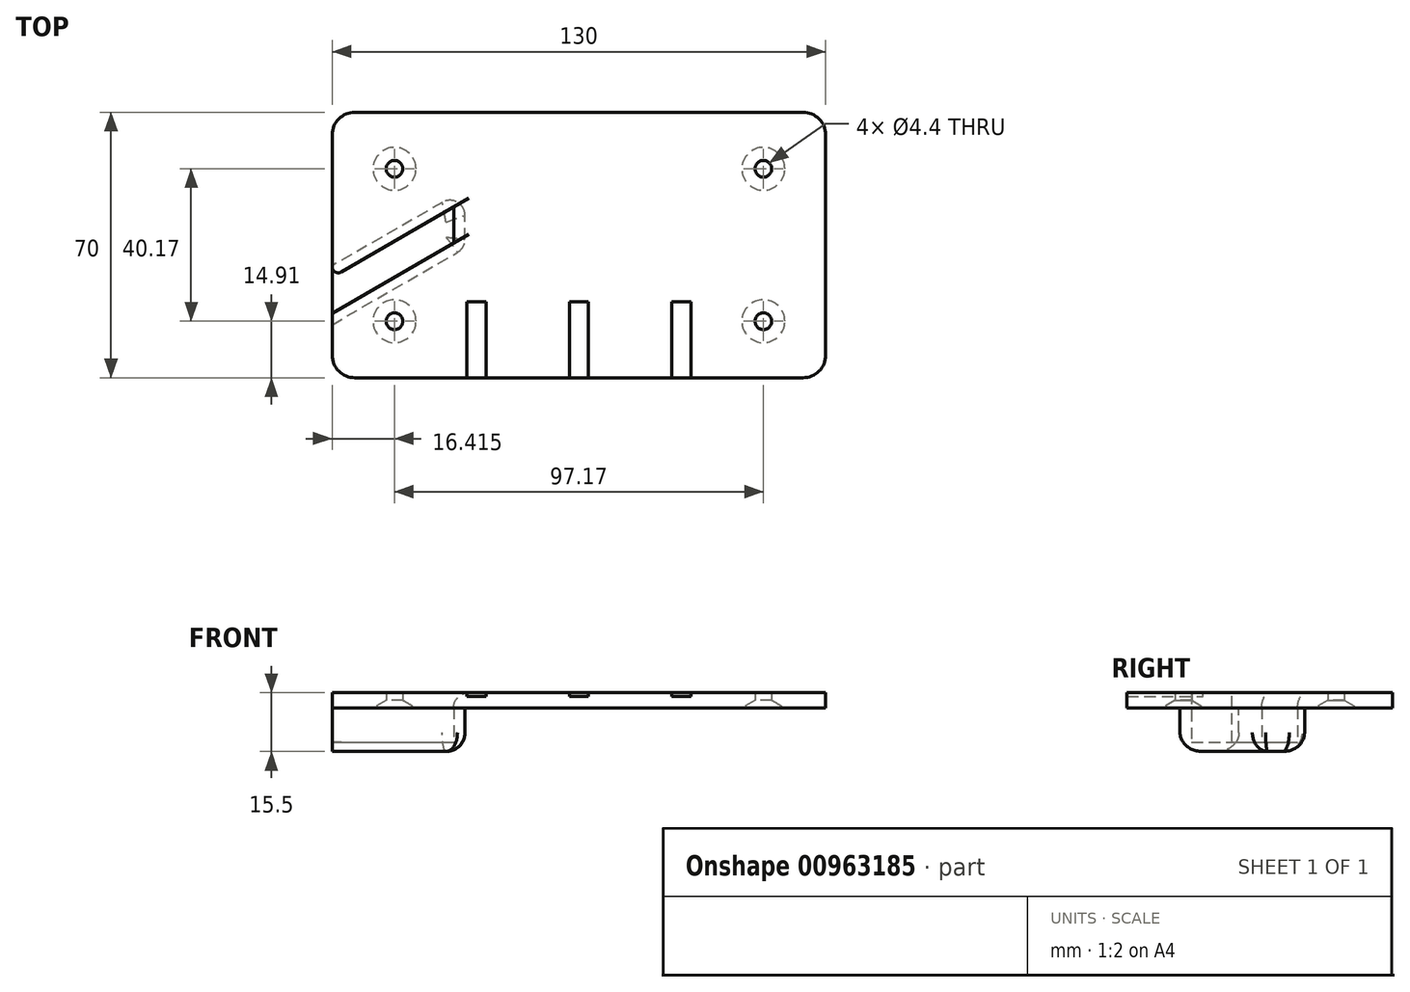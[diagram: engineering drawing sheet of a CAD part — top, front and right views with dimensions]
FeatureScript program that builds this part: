
annotation { "Feature Type Name" : "Feature", "Feature Type Description" : "" }
export const myFeature = defineFeature(function(context is Context, id is Id, definition is map)
    precondition{}
    {
        {
            var Q0;
            Q0=qCreatedBy(makeId("Top.planeOp"),FACE);
            var sketch = newSketch(context, id + "F0", { "sketchPlane" : qUnion([Q0])});
            skLineSegment(sketch, "E0.bottom", {"start": v(-46.53, -21.36) * mm, "end": v(71.47, -21.36) * mm});
            skLineSegment(sketch, "E0.top", {"start": v(-46.53, 48.64) * mm, "end": v(71.47, 48.64) * mm});
            skLineSegment(sketch, "E0.left", {"start": v(-52.53, -15.36) * mm, "end": v(-52.53, 42.64) * mm});
            skLineSegment(sketch, "E0.right", {"start": v(77.47, -15.36) * mm, "end": v(77.47, 42.64) * mm});
            skPoint(sketch, "E1.visualSharp", {"position": v(-52.53, 48.64) * mm});
            skArc(sketch, "E1.filletArc", {"start": v(-46.53, 48.64) * mm, "mid": v(-50.77, 46.88) * mm, "end": v(-52.53, 42.64) * mm});
            skPoint(sketch, "E2.visualSharp", {"position": v(77.47, 48.64) * mm});
            skArc(sketch, "E2.filletArc", {"start": v(77.47, 42.64) * mm, "mid": v(75.71, 46.88) * mm, "end": v(71.47, 48.64) * mm});
            skPoint(sketch, "E3.visualSharp", {"position": v(77.47, -21.36) * mm});
            skArc(sketch, "E3.filletArc", {"start": v(71.47, -21.36) * mm, "mid": v(75.71, -19.6) * mm, "end": v(77.47, -15.36) * mm});
            skPoint(sketch, "E4.visualSharp", {"position": v(-52.53, -21.36) * mm});
            skArc(sketch, "E4.filletArc", {"start": v(-52.53, -15.36) * mm, "mid": v(-50.77, -19.6) * mm, "end": v(-46.53, -21.36) * mm});
            skPoint(sketch, "E5", {"position": v(-36.11, 33.72) * mm});
            skPoint(sketch, "E6", {"position": v(61.06, 33.72) * mm});
            skPoint(sketch, "E7", {"position": v(61.06, -6.45) * mm});
            skPoint(sketch, "E8", {"position": v(-36.11, -6.45) * mm});
            skPoint(sketch, "E9", {"position": v(12.47, -6.45) * mm});
            skPoint(sketch, "E10", {"position": v(61.06, 13.64) * mm});
            skPoint(sketch, "E11", {"position": v(12.47, -21.36) * mm});
            skPoint(sketch, "E12", {"position": v(77.47, 13.64) * mm});
            skCircle(sketch, "E13", {"center": v(61.06, -6.45) * mm, "radius": 2.2 * mm});
            skCircle(sketch, "E14", {"center": v(61.06, 33.72) * mm, "radius": 2.2 * mm});
            skCircle(sketch, "E15", {"center": v(-36.11, 33.72) * mm, "radius": 2.2 * mm});
            skCircle(sketch, "E16", {"center": v(-36.11, -6.45) * mm, "radius": 2.2 * mm});
            skLineSegment(sketch, "E17", {"start": v(-52.53, -4.36) * mm, "end": v(-20.53, 14.11) * mm});
            skLineSegment(sketch, "E18", {"start": v(-52.53, 5.14) * mm, "end": v(-20.53, 23.61) * mm});
            skLineSegment(sketch, "E19", {"start": v(-20.53, 14.11) * mm, "end": v(-20.53, 23.61) * mm});
            skSolve(sketch);
        }
        {
            var Q0;
            Q0=makeQuery(id+"F0.imprint","IMPRINT",FACE,{"disambiguationData":[TD([[makeQuery(id+"F0.imprint","IMPRINT",EDGE,{"derivedFrom":sQuery(id+"F0.wireOp",EDGE,"E0.bottom")}),1.0]])]});
            extrude(context, id + "F1", {"entities" : qUnion([Q0]), "depth" : 4 * mm, "offsetDistance" : 25 * mm});
        }
        {
            var Q0;
            Q0=makeQuery(id+"F1.opExtrude","CAP_FACE",FACE,{"disambiguationData":[OSD([sQuery(id+"F0.wireOp",EDGE,"E0.bottom"),sQuery(id+"F0.wireOp",EDGE,"E0.top"),sQuery(id+"F0.wireOp",EDGE,"E0.left"),sQuery(id+"F0.wireOp",EDGE,"E0.right"),sQuery(id+"F0.wireOp",EDGE,"E1.filletArc"),sQuery(id+"F0.wireOp",EDGE,"E2.filletArc"),sQuery(id+"F0.wireOp",EDGE,"E3.filletArc"),sQuery(id+"F0.wireOp",EDGE,"E4.filletArc"),sQuery(id+"F0.wireOp",EDGE,"E13"),sQuery(id+"F0.wireOp",EDGE,"E14"),sQuery(id+"F0.wireOp",EDGE,"E15"),sQuery(id+"F0.wireOp",EDGE,"E16"),sQuery(id+"F0.wireOp",EDGE,"E17"),sQuery(id+"F0.wireOp",EDGE,"E18"),sQuery(id+"F0.wireOp",EDGE,"E19")])],"isStart":true});
            var sketch = newSketch(context, id + "F2", { "sketchPlane" : qUnion([Q0])});
            skLineSegment(sketch, "E20", {"start": v(-52.53, 7.36) * mm, "end": v(-17.53, -12.84) * mm});
            skLineSegment(sketch, "E21", {"start": v(-17.53, -12.84) * mm, "end": v(-17.53, -28.34) * mm});
            skLineSegment(sketch, "E22", {"start": v(-17.53, -28.34) * mm, "end": v(-52.53, -8.14) * mm});
            skLineSegment(sketch, "E23", {"start": v(-52.53, -8.14) * mm, "end": v(-52.53, -5.14) * mm});
            skLineSegment(sketch, "E24", {"start": v(-52.53, -5.14) * mm, "end": v(-20.53, -23.61) * mm});
            skLineSegment(sketch, "E25", {"start": v(-20.53, -23.61) * mm, "end": v(-20.53, -14.11) * mm});
            skLineSegment(sketch, "E26", {"start": v(-20.53, -14.11) * mm, "end": v(-52.53, 4.36) * mm});
            skLineSegment(sketch, "E27", {"start": v(-52.53, 4.36) * mm, "end": v(-52.53, 7.36) * mm});
            skSolve(sketch);
        }
        {
            var Q0;
            Q0=makeQuery(id+"F2.imprint","IMPRINT",FACE,{"disambiguationData":[TD([[makeQuery(id+"F2.imprint","IMPRINT",EDGE,{"derivedFrom":sQuery(id+"F2.wireOp",EDGE,"E20")}),-1.0]])]});
            extrude(context, id + "F3", {"entities" : qUnion([Q0]), "operationType" : NewBodyOperationType.ADD, "depth" : 9 * mm, "offsetDistance" : 25 * mm});
        }
        {
            var Q0;
            Q0=makeQuery(id+"F1.opExtrude","CAP_EDGE",EDGE,{"disambiguationData":[OSD([sQuery(id+"F0.wireOp",EDGE,"E15")])],"isStart":true});
            var Q1;
            Q1=makeQuery(id+"F1.opExtrude","CAP_EDGE",EDGE,{"disambiguationData":[OSD([sQuery(id+"F0.wireOp",EDGE,"E16")])],"isStart":true});
            var Q2;
            Q2=makeQuery(id+"F1.opExtrude","CAP_EDGE",EDGE,{"disambiguationData":[OSD([sQuery(id+"F0.wireOp",EDGE,"E13")])],"isStart":true});
            var Q3;
            Q3=makeQuery(id+"F1.opExtrude","CAP_EDGE",EDGE,{"disambiguationData":[OSD([sQuery(id+"F0.wireOp",EDGE,"E14")])],"isStart":true});
            chamfer(context, id + "F4", {"entities" : qUnion([Q0, Q1, Q2, Q3]), "chamferType" : ChamferType.OFFSET_ANGLE, "width" : 2 * mm, "oppositeDirection" : true, "angle" : 60 * degree, "tangentPropagation" : true});
        }
        {
            var Q0;
            Q0=makeQuery(id+"F1.opExtrude","CAP_FACE",FACE,{"disambiguationData":[OSD([sQuery(id+"F0.wireOp",EDGE,"E0.bottom"),sQuery(id+"F0.wireOp",EDGE,"E0.top"),sQuery(id+"F0.wireOp",EDGE,"E0.left"),sQuery(id+"F0.wireOp",EDGE,"E0.right"),sQuery(id+"F0.wireOp",EDGE,"E1.filletArc"),sQuery(id+"F0.wireOp",EDGE,"E2.filletArc"),sQuery(id+"F0.wireOp",EDGE,"E3.filletArc"),sQuery(id+"F0.wireOp",EDGE,"E4.filletArc"),sQuery(id+"F0.wireOp",EDGE,"E13"),sQuery(id+"F0.wireOp",EDGE,"E14"),sQuery(id+"F0.wireOp",EDGE,"E15"),sQuery(id+"F0.wireOp",EDGE,"E16"),sQuery(id+"F0.wireOp",EDGE,"E17"),sQuery(id+"F0.wireOp",EDGE,"E18"),sQuery(id+"F0.wireOp",EDGE,"E19")])],"isStart":false});
            var sketch = newSketch(context, id + "F5", { "sketchPlane" : qUnion([Q0])});
            skLineSegment(sketch, "E28.bottom", {"start": v(-17.03, -21.36) * mm, "end": v(-12.03, -21.36) * mm});
            skLineSegment(sketch, "E28.top", {"start": v(-17.03, -1.36) * mm, "end": v(-12.03, -1.36) * mm});
            skLineSegment(sketch, "E28.left", {"start": v(-17.03, -21.36) * mm, "end": v(-17.03, -1.36) * mm});
            skLineSegment(sketch, "E28.right", {"start": v(-12.03, -21.36) * mm, "end": v(-12.03, -1.36) * mm});
            skLineSegment(sketch, "E29.bottom", {"start": v(36.97, -21.36) * mm, "end": v(41.97, -21.36) * mm});
            skLineSegment(sketch, "E29.top", {"start": v(36.97, -1.36) * mm, "end": v(41.97, -1.36) * mm});
            skLineSegment(sketch, "E29.left", {"start": v(36.97, -21.36) * mm, "end": v(36.97, -1.36) * mm});
            skLineSegment(sketch, "E29.right", {"start": v(41.97, -21.36) * mm, "end": v(41.97, -1.36) * mm});
            skPoint(sketch, "E30", {"position": v(-46.53, -21.36) * mm});
            skPoint(sketch, "E31", {"position": v(71.47, -21.36) * mm});
            skPoint(sketch, "E32", {"position": v(12.47, -21.36) * mm});
            skPoint(sketch, "E33", {"position": v(-17.03, -21.36) * mm});
            skPoint(sketch, "E34", {"position": v(41.97, -21.36) * mm});
            skLineSegment(sketch, "E35.bottom", {"start": v(9.97, -21.36) * mm, "end": v(14.97, -21.36) * mm});
            skLineSegment(sketch, "E35.top", {"start": v(9.97, -1.36) * mm, "end": v(14.97, -1.36) * mm});
            skLineSegment(sketch, "E35.left", {"start": v(9.97, -21.36) * mm, "end": v(9.97, -1.36) * mm});
            skLineSegment(sketch, "E35.right", {"start": v(14.97, -21.36) * mm, "end": v(14.97, -1.36) * mm});
            skSolve(sketch);
        }
        {
            var Q0;
            Q0=makeQuery(id+"F5.imprint","IMPRINT",FACE,{"disambiguationData":[TD([[makeQuery(id+"F5.imprint","IMPRINT",EDGE,{"derivedFrom":sQuery(id+"F5.wireOp",EDGE,"E28.bottom")}),1.0]])]});
            var Q1;
            Q1=makeQuery(id+"F5.imprint","IMPRINT",FACE,{"disambiguationData":[TD([[makeQuery(id+"F5.imprint","IMPRINT",EDGE,{"derivedFrom":sQuery(id+"F5.wireOp",EDGE,"E35.bottom")}),1.0]])]});
            var Q2;
            Q2=makeQuery(id+"F5.imprint","IMPRINT",FACE,{"disambiguationData":[TD([[makeQuery(id+"F5.imprint","IMPRINT",EDGE,{"derivedFrom":sQuery(id+"F5.wireOp",EDGE,"E29.bottom")}),1.0]])]});
            extrude(context, id + "F6", {"entities" : qUnion([Q0, Q1, Q2]), "operationType" : NewBodyOperationType.REMOVE, "oppositeDirection" : true, "depth" : 1 * mm, "offsetDistance" : 25 * mm});
        }
        {
            var Q0;
            Q0=makeQuery(id+"F3.opExtrude","CAP_FACE",FACE,{"disambiguationData":[OSD([sQuery(id+"F2.wireOp",EDGE,"E20"),sQuery(id+"F2.wireOp",EDGE,"E21"),sQuery(id+"F2.wireOp",EDGE,"E22"),sQuery(id+"F2.wireOp",EDGE,"E23"),sQuery(id+"F2.wireOp",EDGE,"E24"),sQuery(id+"F2.wireOp",EDGE,"E25"),sQuery(id+"F2.wireOp",EDGE,"E26"),sQuery(id+"F2.wireOp",EDGE,"E27")])],"isStart":false});
            var sketch = newSketch(context, id + "F7", { "sketchPlane" : qUnion([Q0])});
            skLineSegment(sketch, "E36.0", {"start": v(-17.53, -12.84) * mm, "end": v(-17.53, -28.34) * mm});
            skLineSegment(sketch, "E37.0", {"start": v(-52.53, 7.36) * mm, "end": v(-17.53, -12.84) * mm});
            skLineSegment(sketch, "E38.0", {"start": v(-17.53, -28.34) * mm, "end": v(-52.53, -8.14) * mm});
            skLineSegment(sketch, "E39.0", {"start": v(-52.53, -5.14) * mm, "end": v(-52.53, -8.14) * mm});
            skLineSegment(sketch, "E40.0", {"start": v(-52.53, 7.36) * mm, "end": v(-52.53, 4.36) * mm});
            skLineSegment(sketch, "E41", {"start": v(-52.53, 4.36) * mm, "end": v(-52.53, -5.14) * mm});
            skSolve(sketch);
        }
        {
            var Q0;
            Q0=makeQuery(id+"F7.imprint","IMPRINT",FACE,{"disambiguationData":[TD([[makeQuery(id+"F7.imprint","IMPRINT",EDGE,{"derivedFrom":sQuery(id+"F7.wireOp",EDGE,"E41")}),1.0]])]});
            var Q1;
            Q1=makeQuery(id+"F7.imprint","IMPRINT",FACE,{"disambiguationData":[TD([[makeQuery(id+"F7.imprint","IMPRINT",EDGE,{"derivedFrom":sQuery(id+"F7.wireOp",EDGE,"E36.0")}),-1.0]])]});
            extrude(context, id + "F8", {"entities" : qUnion([Q0, Q1]), "operationType" : NewBodyOperationType.ADD, "depth" : 2.5 * mm, "offsetDistance" : 25 * mm});
        }
        {
            var Q0;
            Q0=makeQuery(id+"F3.opExtrude","CAP_EDGE",EDGE,{"disambiguationData":[OSD([sQuery(id+"F2.wireOp",EDGE,"E26")])],"isStart":false});
            var Q1;
            Q1=makeQuery(id+"F3.opExtrude","CAP_EDGE",EDGE,{"disambiguationData":[OSD([sQuery(id+"F2.wireOp",EDGE,"E24")])],"isStart":false});
            var Q2;
            Q2=makeQuery(id+"F3.opExtrude","CAP_EDGE",EDGE,{"disambiguationData":[OSD([sQuery(id+"F2.wireOp",EDGE,"E25")])],"isStart":false});
            var Q3;
            Q3=makeQuery(id+"F1.opExtrude","CAP_EDGE",EDGE,{"disambiguationData":[OSD([sQuery(id+"F0.wireOp",EDGE,"E19")])],"isStart":false});
            var Q4;
            Q4=makeQuery(id+"F3.opExtrude","CAP_EDGE",EDGE,{"disambiguationData":[OSD([sQuery(id+"F2.wireOp",EDGE,"E22")])],"isStart":true});
            var Q5;
            Q5=makeQuery(id+"F3.opExtrude","CAP_EDGE",EDGE,{"disambiguationData":[OSD([sQuery(id+"F2.wireOp",EDGE,"E20")])],"isStart":true});
            var Q6;
            Q6=makeQuery(id+"F3.opExtrude","CAP_EDGE",EDGE,{"disambiguationData":[OSD([sQuery(id+"F2.wireOp",EDGE,"E21")])],"isStart":true});
            fillet(context, id + "F9", {"entities" : qUnion([Q0, Q1, Q2, Q3, Q4, Q5, Q6]), "radius" : 4 * mm, "tangentPropagation" : true, "allowEdgeOverflow" : false});
        }
        {
            var Q0;
            Q0=makeQuery(id+"F8.opExtrude","CAP_EDGE",EDGE,{"disambiguationData":[OSD([sQuery(id+"F7.wireOp",EDGE,"E38.0")])],"isStart":false});
            var Q1;
            Q1=makeQuery(id+"F8.opExtrude","CAP_EDGE",EDGE,{"disambiguationData":[OSD([sQuery(id+"F7.wireOp",EDGE,"E37.0")])],"isStart":false});
            var Q2;
            Q2=makeQuery(id+"F8.opExtrude","CAP_EDGE",EDGE,{"disambiguationData":[OSD([sQuery(id+"F7.wireOp",EDGE,"E36.0")])],"isStart":false});
            fillet(context, id + "F10", {"entities" : qUnion([Q0, Q1, Q2]), "radius" : 5 * mm, "tangentPropagation" : true, "allowEdgeOverflow" : false});
        }
        {
            var Q0;
            Q0=makeQuery(id+"F10.opFillet","BLEND_EDGE",EDGE,{"blendedFrom":[makeQuery(id+"F8.opExtrude","CAP_EDGE",EDGE,{"disambiguationData":[OSD([sQuery(id+"F7.wireOp",EDGE,"E36.0")])],"isStart":false}),makeQuery(id+"F8.opExtrude","CAP_EDGE",EDGE,{"disambiguationData":[OSD([sQuery(id+"F7.wireOp",EDGE,"E38.0")])],"isStart":false})],"blendedInto":[]});
            var Q1;
            Q1=makeQuery(id+"F10.opFillet","BLEND_EDGE",EDGE,{"blendedFrom":[makeQuery(id+"F8.opExtrude","CAP_EDGE",EDGE,{"disambiguationData":[OSD([sQuery(id+"F7.wireOp",EDGE,"E36.0")])],"isStart":false}),makeQuery(id+"F8.opExtrude","CAP_EDGE",EDGE,{"disambiguationData":[OSD([sQuery(id+"F7.wireOp",EDGE,"E37.0")])],"isStart":false})],"blendedInto":[]});
            var Q2;
            Q2=makeQuery(id+"F9.opFillet","BLEND_EDGE",EDGE,{"blendedFrom":[makeQuery(id+"F3.opExtrude","CAP_EDGE",EDGE,{"disambiguationData":[OSD([sQuery(id+"F2.wireOp",EDGE,"E25")])],"isStart":false}),makeQuery(id+"F3.opExtrude","CAP_EDGE",EDGE,{"disambiguationData":[OSD([sQuery(id+"F2.wireOp",EDGE,"E26")])],"isStart":false})],"blendedInto":[]});
            var Q3;
            Q3=makeQuery(id+"F9.opFillet","BLEND_EDGE",EDGE,{"blendedFrom":[makeQuery(id+"F3.opExtrude","CAP_EDGE",EDGE,{"disambiguationData":[OSD([sQuery(id+"F2.wireOp",EDGE,"E24")])],"isStart":false}),makeQuery(id+"F3.opExtrude","CAP_EDGE",EDGE,{"disambiguationData":[OSD([sQuery(id+"F2.wireOp",EDGE,"E25")])],"isStart":false})],"blendedInto":[]});
            fillet(context, id + "F11", {"entities" : qUnion([Q0, Q1, Q2, Q3]), "radius" : 4 * mm, "tangentPropagation" : true, "allowEdgeOverflow" : false});
        }
        {
            var Q0;
            Q0=makeQuery(id+"F3.boolean.opBoolean","MERGE",EDGE,{"derivedFrom":[makeQuery(id+"F1.opExtrude","SWEPT_EDGE",EDGE,{"disambiguationData":[OSD([sQuery(id+"F0.wireOp",EDGE,"E0.left"),sQuery(id+"F0.wireOp",EDGE,"E18")])]}),makeQuery(id+"F3.opExtrude","SWEPT_EDGE",EDGE,{"disambiguationData":[OSD([sQuery(id+"F2.wireOp",EDGE,"E23"),sQuery(id+"F2.wireOp",EDGE,"E24")])]})]});
            fillet(context, id + "F12", {"entities" : qUnion([Q0]), "radius" : 1.6 * mm, "tangentPropagation" : true, "allowEdgeOverflow" : false});
        }
    });
